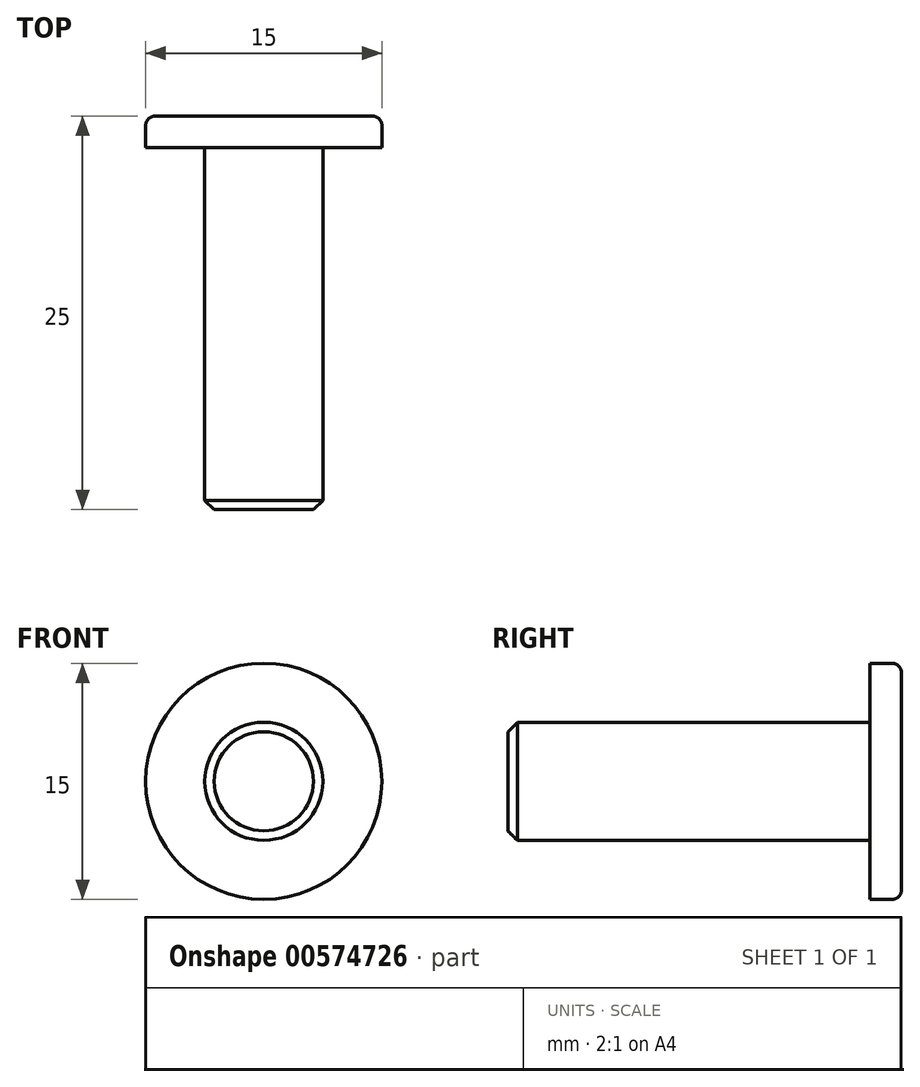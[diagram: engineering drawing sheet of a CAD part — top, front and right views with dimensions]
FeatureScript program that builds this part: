
annotation { "Feature Type Name" : "Feature", "Feature Type Description" : "" }
export const myFeature = defineFeature(function(context is Context, id is Id, definition is map)
    precondition{}
    {
        {
            var Q0;
            Q0=qCreatedBy(makeId("Front.planeOp"),FACE);
            var sketch = newSketch(context, id + "F0", { "sketchPlane" : qUnion([Q0])});
            skCircle(sketch, "E0", {"center": v(0, 0) * mm, "radius": 3.75 * mm});
            skSolve(sketch);
        }
        {
            var Q0;
            Q0=makeQuery(id+"F0.imprint","IMPRINT",FACE,{"disambiguationData":[TD([[makeQuery(id+"F0.imprint","IMPRINT",EDGE,{"derivedFrom":sQuery(id+"F0.wireOp",EDGE,"E0")}),1.0]])]});
            extrude(context, id + "F1", {"entities" : qUnion([Q0]), "depth" : 25 * mm, "offsetDistance" : 25 * mm});
        }
        {
            var Q0;
            Q0=qCreatedBy(makeId("Front.planeOp"),FACE);
            var sketch = newSketch(context, id + "F2", { "sketchPlane" : qUnion([Q0])});
            skCircle(sketch, "E1", {"center": v(0, 0) * mm, "radius": 7.5 * mm});
            skSolve(sketch);
        }
        {
            var Q0;
            Q0=makeQuery(id+"F2.imprint","IMPRINT",FACE,{"disambiguationData":[TD([[makeQuery(id+"F2.imprint","IMPRINT",EDGE,{"derivedFrom":sQuery(id+"F2.wireOp",EDGE,"E1")}),1.0]])]});
            extrude(context, id + "F3", {"entities" : qUnion([Q0]), "operationType" : NewBodyOperationType.ADD, "depth" : 2 * mm, "offsetDistance" : 25 * mm});
        }
        {
            var Q0;
            Q0=makeQuery(id+"F3.opExtrude","CAP_EDGE",EDGE,{"disambiguationData":[OSD([sQuery(id+"F2.wireOp",EDGE,"E1")])],"isStart":true});
            fillet(context, id + "F4", {"entities" : qUnion([Q0]), "radius" : 0.6 * mm, "tangentPropagation" : true, "allowEdgeOverflow" : false});
        }
        {
            var Q0;
            Q0=makeQuery(id+"F1.opExtrude","CAP_EDGE",EDGE,{"disambiguationData":[OSD([sQuery(id+"F0.wireOp",EDGE,"E0")])],"isStart":false});
            chamfer(context, id + "F5", {"entities" : qUnion([Q0]), "width" : 0.6 * mm, "tangentPropagation" : true});
        }
    });
